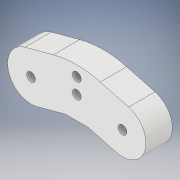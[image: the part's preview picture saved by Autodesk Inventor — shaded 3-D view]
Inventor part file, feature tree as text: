
AUTODESK INVENTOR PART (.ipt)
format: ipt  version: 2017 SP1 (Build 210196100, 196)  size: 135,168 bytes
history: native  units: in
note: dims shown in document units (in); Inventor stores cm internally (conversion verified against a paired STEP export)
features: extrude x2, sketch x2
ambient origin geometry x8: Origin, YZ Plane, XZ Plane, XY Plane, X Axis, Y Axis, Z Axis, Center Point
bodies: Solid1 (feature_tree)
feature tree (4):
  extrude  "Extrusion1"  Depth=0.6299in
  extrude  "Extrusion3"  Depth=0.3543in
  sketch  "Sketch1"  dims[d0=0.6299in d1=0.6299in d2=0.6299in d3=0.3937in d4=0.3937in d5=0.6299in d6=0.6299in d7=75.0deg d8=0.1181in]
  sketch  "Sketch3"  dims[d9=0.1181in d10=0.1181in d11=0.5118in d12=0.3543in d13=0.0in d19=0.1181in d20=0.1181in d21=0.0in]
